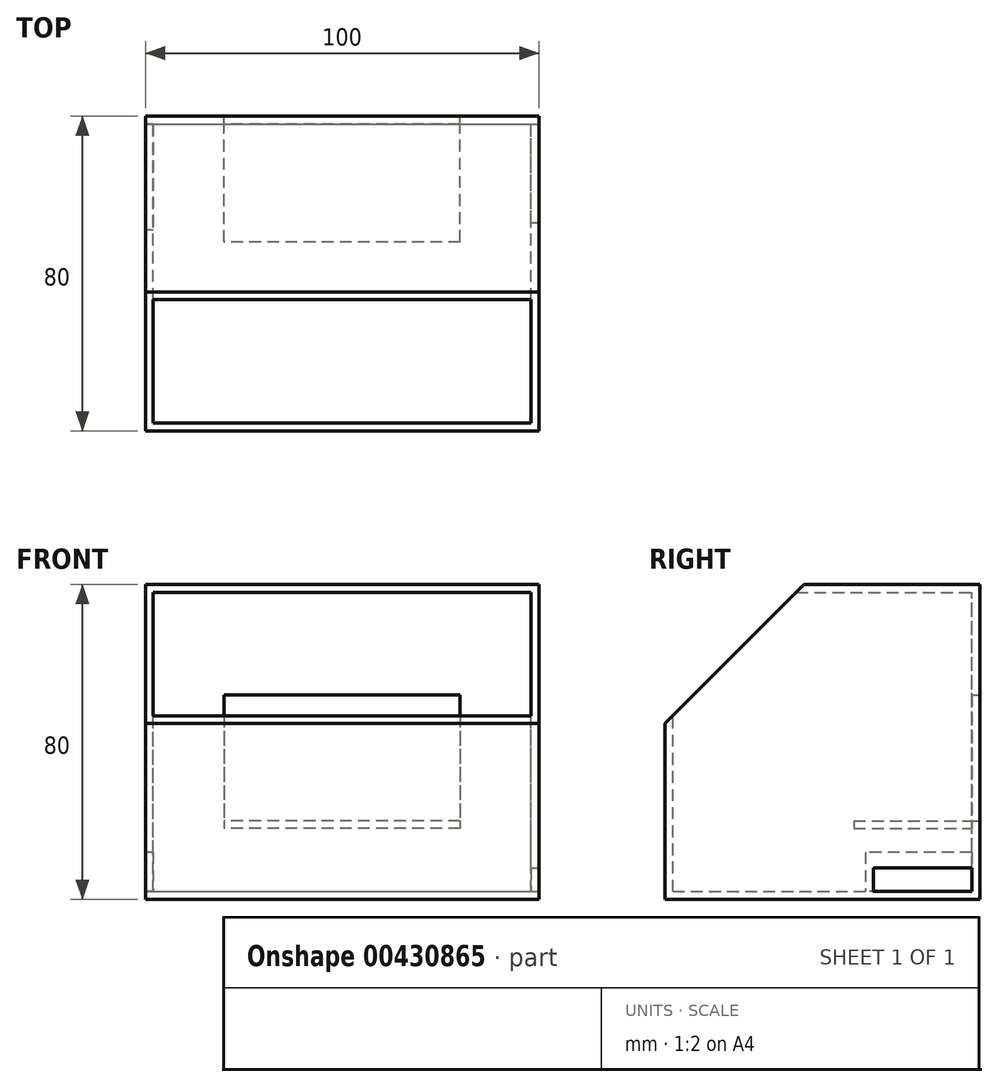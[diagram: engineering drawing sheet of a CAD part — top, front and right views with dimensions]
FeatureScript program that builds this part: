
annotation { "Feature Type Name" : "Feature", "Feature Type Description" : "" }
export const myFeature = defineFeature(function(context is Context, id is Id, definition is map)
    precondition{}
    {
        {
            var Q0;
            Q0=qCreatedBy(makeId("Right.planeOp"),FACE);
            var sketch = newSketch(context, id + "F0", { "sketchPlane" : qUnion([Q0])});
            skLineSegment(sketch, "E0.bottom", {"start": v(-49.91, -15.45) * mm, "end": v(30.09, -15.45) * mm});
            skLineSegment(sketch, "E0.top", {"start": v(-49.91, 64.55) * mm, "end": v(30.09, 64.55) * mm});
            skLineSegment(sketch, "E0.left", {"start": v(-49.91, -15.45) * mm, "end": v(-49.91, 64.55) * mm});
            skLineSegment(sketch, "E0.right", {"start": v(30.09, -15.45) * mm, "end": v(30.09, 64.55) * mm});
            skLineSegment(sketch, "E1", {"start": v(-49.91, 29.2) * mm, "end": v(-14.56, 64.55) * mm});
            skLineSegment(sketch, "E2.bottom", {"start": v(3.09, -7.45) * mm, "end": v(28.09, -7.45) * mm});
            skLineSegment(sketch, "E2.top", {"start": v(3.09, -13.45) * mm, "end": v(28.09, -13.45) * mm});
            skLineSegment(sketch, "E2.left", {"start": v(3.09, -7.45) * mm, "end": v(3.09, -13.45) * mm});
            skLineSegment(sketch, "E2.right", {"start": v(28.09, -7.45) * mm, "end": v(28.09, -13.45) * mm});
            skSolve(sketch);
        }
        {
            var Q0;
            Q0=makeQuery(id+"F0.imprint","IMPRINT",FACE,{"disambiguationData":[TD([[makeQuery(id+"F0.imprint","IMPRINT",EDGE,{"derivedFrom":sQuery(id+"F0.wireOp",EDGE,"E2.bottom")}),-1.0]])]});
            var Q1;
            {var subQ1=sQuery(id+"F0.wireOp",EDGE,"E0.bottom");Q1=makeQuery(id+"F0.imprint","IMPRINT",FACE,{"disambiguationData":[TD([[makeQuery(id+"F0.imprint","IMPRINT",EDGE,{"derivedFrom":subQ1}),1.0]])]});}
            extrude(context, id + "F1", {"entities" : qUnion([Q0, Q1]), "oppositeDirection" : true, "depth" : 100 * mm});
        }
        {
            var Q0;
            Q0=makeQuery(id+"F1.opExtrude","SWEPT_FACE",FACE,{"disambiguationData":[OSD([sQuery(id+"F0.wireOp",EDGE,"E1")])]});
            var Q1;
            Q1=makeQuery(id+"F1.opExtrude","SWEPT_BODY",BODY,{"disambiguationData":[OSD([sQuery(id+"F0.wireOp",EDGE,"E0.bottom"),sQuery(id+"F0.wireOp",EDGE,"E0.top"),sQuery(id+"F0.wireOp",EDGE,"E0.left"),sQuery(id+"F0.wireOp",EDGE,"E0.right"),sQuery(id+"F0.wireOp",EDGE,"E1")])]});
            shell(context, id + "F2", {"entities" : qUnion([Q0]), "parts" : qUnion([Q1]), "thickness" : 2 * mm});
        }
        {
            var Q0;
            Q0=makeQuery(id+"F0.imprint","IMPRINT",FACE,{"disambiguationData":[TD([[makeQuery(id+"F0.imprint","IMPRINT",EDGE,{"derivedFrom":sQuery(id+"F0.wireOp",EDGE,"E2.bottom")}),-1.0]])]});
            extrude(context, id + "F3", {"entities" : qUnion([Q0]), "operationType" : NewBodyOperationType.REMOVE, "oppositeDirection" : true, "depth" : 2 * mm});
        }
        {
            var Q0;
            Q0=makeQuery(id+"F1.opExtrude","CAP_FACE",FACE,{"disambiguationData":[OSD([sQuery(id+"F0.wireOp",EDGE,"E0.bottom"),sQuery(id+"F0.wireOp",EDGE,"E0.top"),sQuery(id+"F0.wireOp",EDGE,"E0.left"),sQuery(id+"F0.wireOp",EDGE,"E0.right"),sQuery(id+"F0.wireOp",EDGE,"E1")])],"isStart":false});
            var sketch = newSketch(context, id + "F4", { "sketchPlane" : qUnion([Q0])});
            skLineSegment(sketch, "E3.bottom", {"start": v(-28.09, -3.45) * mm, "end": v(-1.09, -3.45) * mm});
            skLineSegment(sketch, "E3.top", {"start": v(-28.09, -13.45) * mm, "end": v(-1.09, -13.45) * mm});
            skLineSegment(sketch, "E3.left", {"start": v(-28.09, -3.45) * mm, "end": v(-28.09, -13.45) * mm});
            skLineSegment(sketch, "E3.right", {"start": v(-1.09, -3.45) * mm, "end": v(-1.09, -13.45) * mm});
            skSolve(sketch);
        }
        {
            var Q0;
            Q0=makeQuery(id+"F4.imprint","IMPRINT",FACE,{"disambiguationData":[TD([[makeQuery(id+"F4.imprint","IMPRINT",EDGE,{"derivedFrom":sQuery(id+"F4.wireOp",EDGE,"E3.bottom")}),-1.0]])]});
            extrude(context, id + "F5", {"entities" : qUnion([Q0]), "operationType" : NewBodyOperationType.REMOVE, "oppositeDirection" : true, "depth" : 2 * mm});
        }
        {
            var Q0;
            Q0=makeQuery(id+"F1.opExtrude","SWEPT_FACE",FACE,{"disambiguationData":[OSD([sQuery(id+"F0.wireOp",EDGE,"E0.right")])]});
            var sketch = newSketch(context, id + "F6", { "sketchPlane" : qUnion([Q0])});
            skLineSegment(sketch, "E4.bottom", {"start": v(20, 36.55) * mm, "end": v(80, 36.55) * mm});
            skLineSegment(sketch, "E4.top", {"start": v(20, 4.55) * mm, "end": v(80, 4.55) * mm});
            skLineSegment(sketch, "E4.left", {"start": v(20, 36.55) * mm, "end": v(20, 4.55) * mm});
            skLineSegment(sketch, "E4.right", {"start": v(80, 36.55) * mm, "end": v(80, 4.55) * mm});
            skLineSegment(sketch, "E5.top", {"start": v(20, 2.55) * mm, "end": v(80, 2.55) * mm});
            skLineSegment(sketch, "E5.left", {"start": v(20, 4.55) * mm, "end": v(20, 2.55) * mm});
            skLineSegment(sketch, "E5.right", {"start": v(80, 4.55) * mm, "end": v(80, 2.55) * mm});
            skSolve(sketch);
        }
        {
            var Q0;
            Q0=makeQuery(id+"F6.imprint","IMPRINT",FACE,{"disambiguationData":[TD([[makeQuery(id+"F6.imprint","IMPRINT",EDGE,{"derivedFrom":sQuery(id+"F6.wireOp",EDGE,"E4.bottom")}),-1.0]])]});
            extrude(context, id + "F7", {"entities" : qUnion([Q0]), "operationType" : NewBodyOperationType.REMOVE, "oppositeDirection" : true, "depth" : 2 * mm});
        }
        {
            var Q0;
            Q0=makeQuery(id+"F6.imprint","IMPRINT",FACE,{"disambiguationData":[TD([[makeQuery(id+"F6.imprint","IMPRINT",EDGE,{"derivedFrom":sQuery(id+"F6.wireOp",EDGE,"E4.top")}),-1.0]])]});
            extrude(context, id + "F8", {"entities" : qUnion([Q0]), "operationType" : NewBodyOperationType.ADD, "oppositeDirection" : true, "depth" : (30 + 2) * mm});
        }
    });
